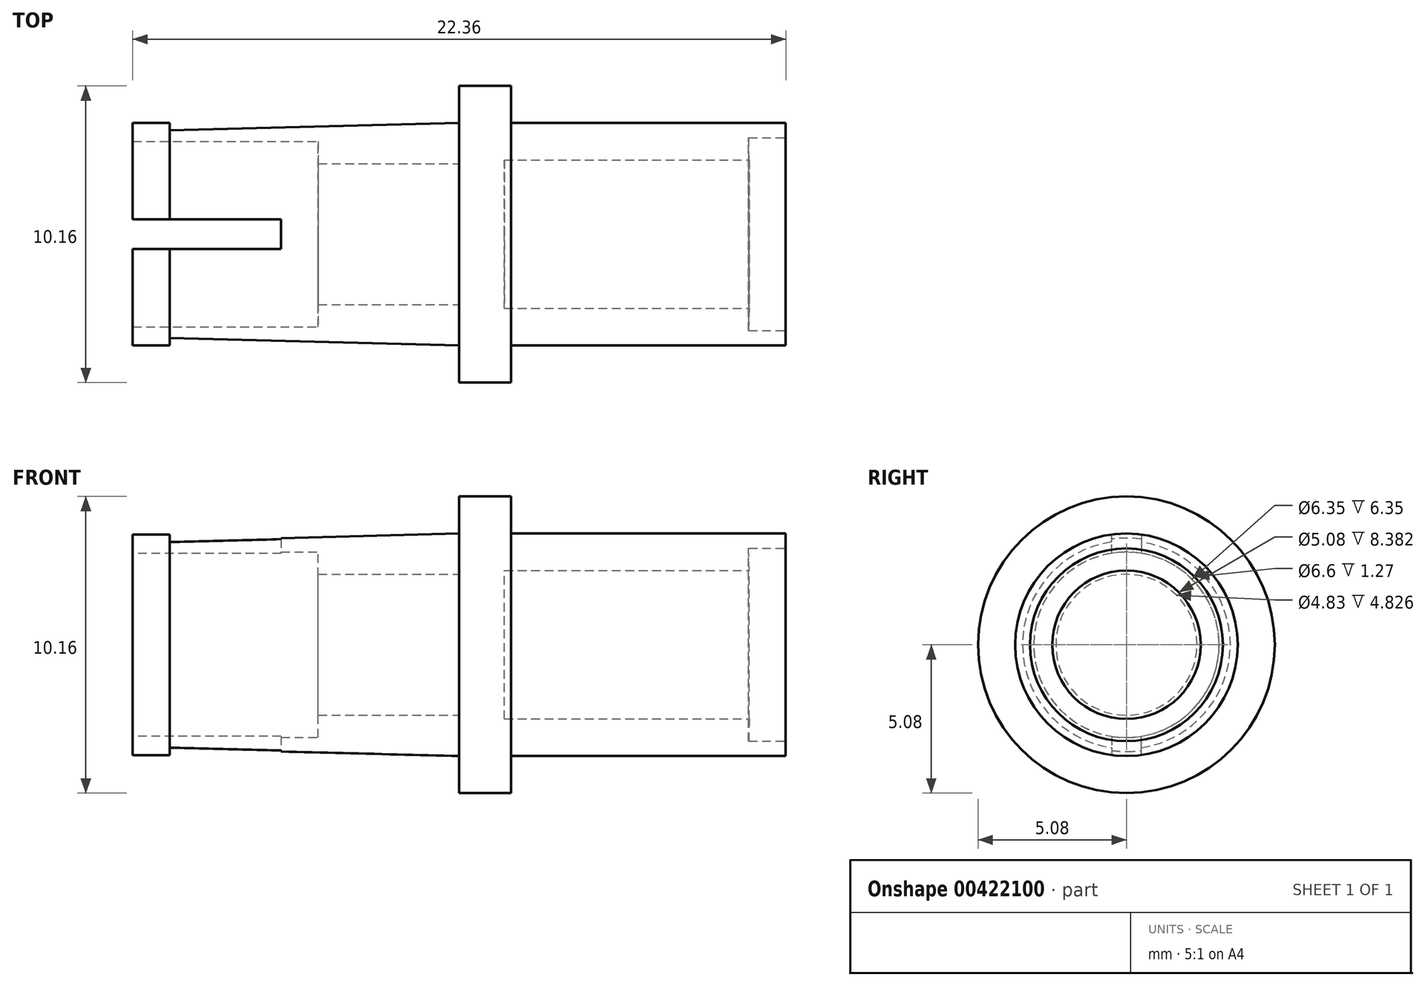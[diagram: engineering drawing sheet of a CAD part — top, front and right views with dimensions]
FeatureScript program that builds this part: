
annotation { "Feature Type Name" : "Feature", "Feature Type Description" : "" }
export const myFeature = defineFeature(function(context is Context, id is Id, definition is map)
    precondition{}
    {
        {
            var Q0;
            Q0=qCreatedBy(makeId("Front.planeOp"),FACE);
            var sketch = newSketch(context, id + "F0", { "sketchPlane" : qUnion([Q0])});
            skLineSegment(sketch, "E0", {"start": v(0, 0) * mm, "end": v(0, 2.41) * mm});
            skLineSegment(sketch, "E1", {"start": v(0, 2.41) * mm, "end": v(-4.83, 2.41) * mm});
            skLineSegment(sketch, "E2", {"start": v(-4.83, 2.41) * mm, "end": v(-4.83, 3.17) * mm});
            skLineSegment(sketch, "E3", {"start": v(-4.83, 3.17) * mm, "end": v(-11.18, 3.17) * mm});
            skLineSegment(sketch, "E4", {"start": v(-11.18, 3.17) * mm, "end": v(-11.18, 3.8) * mm});
            skLineSegment(sketch, "E5", {"start": v(-11.18, 3.8) * mm, "end": v(-9.9, 3.8) * mm});
            skLineSegment(sketch, "E6", {"start": v(-9.9, 3.8) * mm, "end": v(-9.9, 3.56) * mm});
            skLineSegment(sketch, "E7", {"start": v(-9.9, 3.56) * mm, "end": v(-9.9, 3.8) * mm});
            skLineSegment(sketch, "E8", {"start": v(0, 3.8) * mm, "end": v(-9.9, 3.56) * mm});
            skLineSegment(sketch, "E9", {"start": v(0, 3.8) * mm, "end": v(0, 5.08) * mm});
            skLineSegment(sketch, "E10", {"start": v(0, 5.08) * mm, "end": v(1.78, 5.08) * mm});
            skLineSegment(sketch, "E11", {"start": v(1.78, 5.08) * mm, "end": v(1.78, 3.8) * mm});
            skLineSegment(sketch, "E12", {"start": v(1.78, 3.8) * mm, "end": v(11.18, 3.8) * mm});
            skLineSegment(sketch, "E13", {"start": v(11.18, 3.81) * mm, "end": v(11.18, 3.3) * mm});
            skLineSegment(sketch, "E14", {"start": v(11.18, 3.3) * mm, "end": v(9.9, 3.3) * mm});
            skLineSegment(sketch, "E15", {"start": v(9.9, 3.3) * mm, "end": v(9.93, 2.54) * mm});
            skLineSegment(sketch, "E16", {"start": v(9.93, 2.54) * mm, "end": v(1.54, 2.54) * mm});
            skLineSegment(sketch, "E17", {"start": v(1.54, 2.54) * mm, "end": v(1.54, 0) * mm});
            skLineSegment(sketch, "E18", {"start": v(1.54, 0) * mm, "end": v(0, 0) * mm});
            skSolve(sketch);
        }
        {
            var Q0;
            Q0=makeQuery(id+"F0.imprint","IMPRINT",FACE,{"disambiguationData":[TD([[makeQuery(id+"F0.imprint","IMPRINT",EDGE,{"derivedFrom":sQuery(id+"F0.wireOp",EDGE,"E0")}),-1.0]])]});
            var Q1;
            Q1=sQuery(id+"F0.wireOp",EDGE,"E18");
            revolve(context, id + "F1", {"entities" : qUnion([Q0]), "axis" : qUnion([Q1]), "revolveType" : RevolveType.FULL});
        }
        {
            var Q0;
            Q0=makeQuery(id+"F1.opRevolve","SWEPT_FACE",FACE,{"disambiguationData":[OSD([sQuery(id+"F0.wireOp",EDGE,"E4")])]});
            var sketch = newSketch(context, id + "F2", { "sketchPlane" : qUnion([Q0])});
            skLineSegment(sketch, "E19", {"start": v(0, 0) * mm, "end": v(0, 3.8) * mm});
            skLineSegment(sketch, "E20", {"start": v(0, 3.8) * mm, "end": v(0.5, 3.8) * mm});
            skLineSegment(sketch, "E21", {"start": v(0.5, 3.8) * mm, "end": v(-0.5, 3.8) * mm});
            skLineSegment(sketch, "E22", {"start": v(-0.5, 3.8) * mm, "end": v(-0.5, 3.13) * mm});
            skLineSegment(sketch, "E23", {"start": v(-0.5, 3.13) * mm, "end": v(0.5, 3.13) * mm});
            skLineSegment(sketch, "E24", {"start": v(0.5, 3.13) * mm, "end": v(0.5, 3.8) * mm});
            skLineSegment(sketch, "E25", {"start": v(0, 0) * mm, "end": v(0, -3.8) * mm});
            skLineSegment(sketch, "E26", {"start": v(0, -3.8) * mm, "end": v(0.5, -3.8) * mm});
            skLineSegment(sketch, "E27", {"start": v(0.5, -3.8) * mm, "end": v(-0.5, -3.8) * mm});
            skLineSegment(sketch, "E28", {"start": v(-0.5, -3.8) * mm, "end": v(-0.5, -3.13) * mm});
            skLineSegment(sketch, "E29", {"start": v(-0.5, -3.13) * mm, "end": v(0.5, -3.13) * mm});
            skLineSegment(sketch, "E30", {"start": v(0.5, -3.13) * mm, "end": v(0.5, -3.8) * mm});
            skSolve(sketch);
        }
        {
            var Q0;
            Q0 = qSketchRegion(id + "F2", true);
            extrude(context, id + "F3", {"entities" : qUnion([Q0]), "operationType" : NewBodyOperationType.REMOVE, "oppositeDirection" : true, "depth" : 5.08 * mm});
        }
    });
